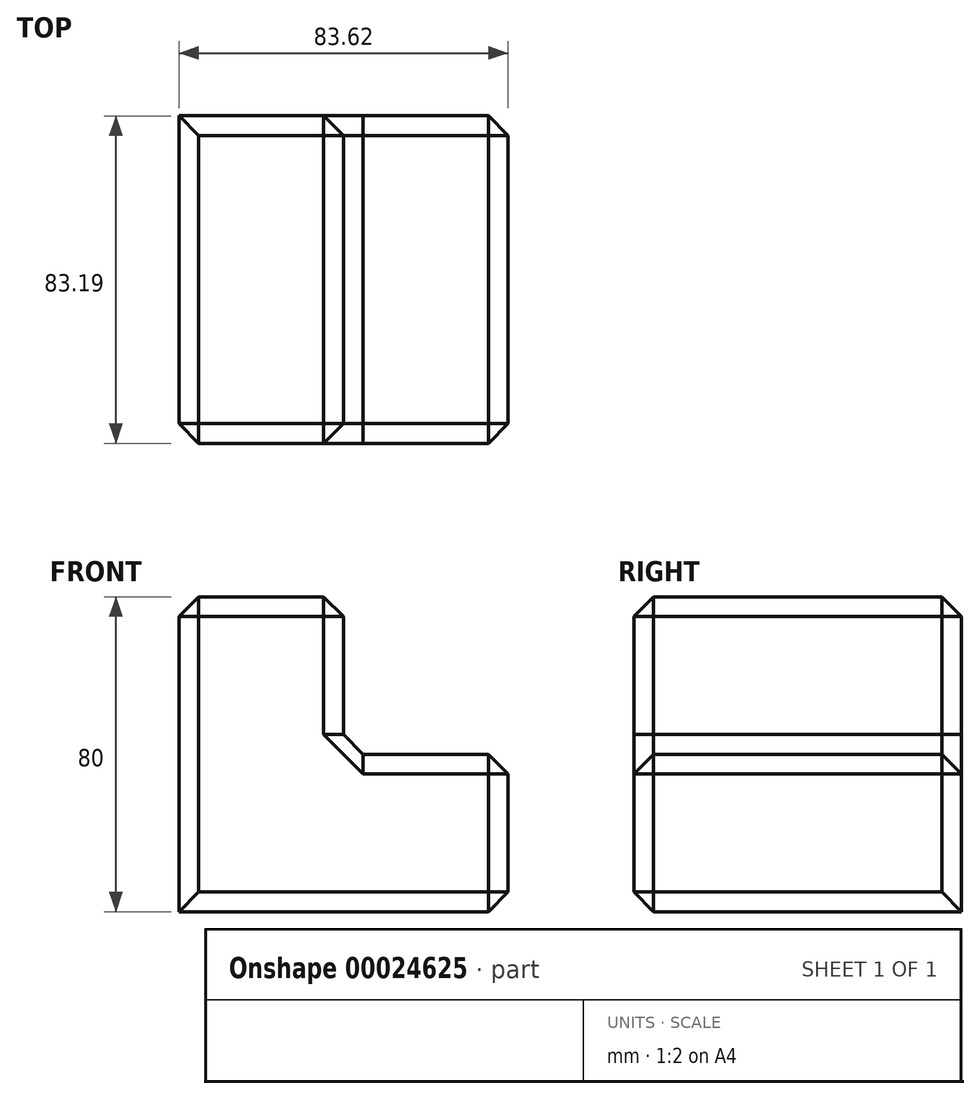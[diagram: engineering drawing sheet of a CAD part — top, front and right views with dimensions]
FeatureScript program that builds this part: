
annotation { "Feature Type Name" : "Feature", "Feature Type Description" : "" }
export const myFeature = defineFeature(function(context is Context, id is Id, definition is map)
    precondition{}
    {
        {
            var Q0;
            Q0=qCreatedBy(makeId("Top.planeOp"),FACE);
            var sketch = newSketch(context, id + "F0", { "sketchPlane" : qUnion([Q0])});
            skLineSegment(sketch, "E0.bottom", {"start": v(-59.13, -45.93) * mm, "end": v(24.5, -45.93) * mm});
            skLineSegment(sketch, "E0.top", {"start": v(-59.13, 37.26) * mm, "end": v(24.5, 37.26) * mm});
            skLineSegment(sketch, "E0.left", {"start": v(-59.13, -45.93) * mm, "end": v(-59.13, 37.26) * mm});
            skLineSegment(sketch, "E0.right", {"start": v(24.5, -45.93) * mm, "end": v(24.5, 37.26) * mm});
            skSolve(sketch);
        }
        {
            var Q0;
            Q0=makeQuery(id+"F0.imprint","IMPRINT",FACE,{"disambiguationData":[TD([[makeQuery(id+"F0.imprint","IMPRINT",EDGE,{"derivedFrom":sQuery(id+"F0.wireOp",EDGE,"E0.bottom")}),1.0]])]});
            extrude(context, id + "F1", {"entities" : qUnion([Q0]), "depth" : 40 * mm});
        }
        {
            var Q0;
            Q0=makeQuery(id+"F1.opExtrude","CAP_FACE",FACE,{"disambiguationData":[OSD([sQuery(id+"F0.wireOp",EDGE,"E0.bottom"),sQuery(id+"F0.wireOp",EDGE,"E0.top"),sQuery(id+"F0.wireOp",EDGE,"E0.left"),sQuery(id+"F0.wireOp",EDGE,"E0.right")])],"isStart":false});
            var sketch = newSketch(context, id + "F2", { "sketchPlane" : qUnion([Q0])});
            skLineSegment(sketch, "E1", {"start": v(-17.32, 37.26) * mm, "end": v(-17.32, -45.93) * mm});
            skSolve(sketch);
        }
        {
            var Q0;
            {var subQ1=sQuery(id+"F2.wireOp",EDGE,"E1");Q0=makeQuery(id+"F2.imprint","IMPRINT",FACE,{"disambiguationData":[TD([[makeQuery(id+"F2.imprint","IMPRINT",EDGE,{"derivedFrom":subQ1}),-1.0]])]});}
            extrude(context, id + "F3", {"entities" : qUnion([Q0]), "operationType" : NewBodyOperationType.ADD, "depth" : 40 * mm});
        }
        {
            var Q0;
            Q0=makeQuery(id+"F3.opExtrude","SWEPT_FACE",FACE,{"disambiguationData":[OSD([sQuery(id+"F2.wireOp",EDGE,"E1")])]});
            var Q1;
            {var subQ0=sQuery(id+"F0.wireOp",EDGE,"E0.bottom");Q1=makeQuery(id+"F3.boolean.opBoolean","MERGE",FACE,{"derivedFrom":[makeQuery(id+"F1.opExtrude","SWEPT_FACE",FACE,{"disambiguationData":[OSD([subQ0])]}),makeQuery(id+"F3.opExtrude","SWEPT_FACE",FACE,{"disambiguationData":[OSD([subQ0])]})]});}
            var Q2;
            Q2=makeQuery(id+"F3.opExtrude","CAP_FACE",FACE,{"disambiguationData":[OSD([sQuery(id+"F0.wireOp",EDGE,"E0.bottom"),sQuery(id+"F0.wireOp",EDGE,"E0.top"),sQuery(id+"F0.wireOp",EDGE,"E0.left"),sQuery(id+"F2.wireOp",EDGE,"E1")])],"isStart":false});
            var Q3;
            Q3=makeQuery(id+"F1.opExtrude","SWEPT_FACE",FACE,{"disambiguationData":[OSD([sQuery(id+"F0.wireOp",EDGE,"E0.right")])]});
            var Q4;
            Q4=makeQuery(id+"F1.opExtrude","CAP_FACE",FACE,{"disambiguationData":[OSD([sQuery(id+"F0.wireOp",EDGE,"E0.bottom"),sQuery(id+"F0.wireOp",EDGE,"E0.top"),sQuery(id+"F0.wireOp",EDGE,"E0.left"),sQuery(id+"F0.wireOp",EDGE,"E0.right")])],"isStart":false});
            chamfer(context, id + "F4", {"entities" : qUnion([Q0, Q1, Q2, Q3, Q4]), "width" : 5 * mm, "tangentPropagation" : true});
        }
    });
